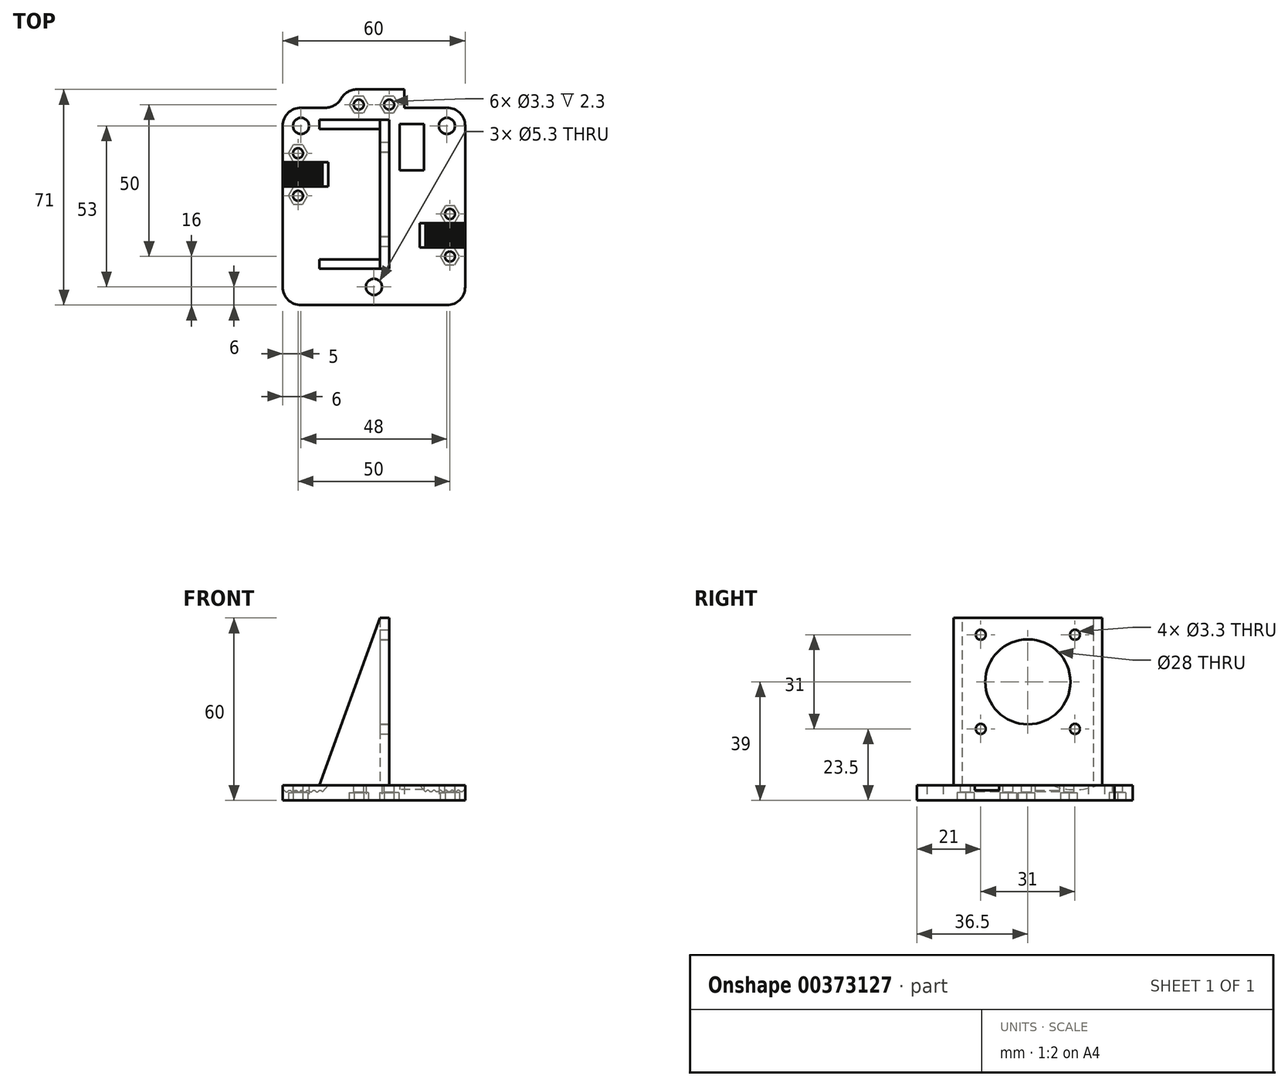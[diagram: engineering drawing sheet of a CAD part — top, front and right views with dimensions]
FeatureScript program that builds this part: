
annotation { "Feature Type Name" : "Feature", "Feature Type Description" : "" }
export const myFeature = defineFeature(function(context is Context, id is Id, definition is map)
    precondition{}
    {
        {
            var Q0;
            Q0=qCreatedBy(makeId("Top.planeOp"),FACE);
            var sketch = newSketch(context, id + "F0", { "sketchPlane" : qUnion([Q0])});
            skLineSegment(sketch, "E0.bottom", {"start": v(0, 0) * mm, "end": v(60, 0) * mm});
            skLineSegment(sketch, "E0.top", {"start": v(0, 65) * mm, "end": v(60, 65) * mm});
            skLineSegment(sketch, "E0.left", {"start": v(0, 0) * mm, "end": v(0, 65) * mm});
            skLineSegment(sketch, "E0.right", {"start": v(60, 0) * mm, "end": v(60, 65) * mm});
            skCircle(sketch, "E1", {"center": v(54, 59) * mm, "radius": 2.65 * mm});
            skCircle(sketch, "E2", {"center": v(6, 59) * mm, "radius": 2.65 * mm});
            skPoint(sketch, "E3.centerSnap0", {"position": v(30, 65) * mm});
            skCircle(sketch, "E4", {"center": v(30, 6) * mm, "radius": 2.65 * mm});
            skPoint(sketch, "E4.centerSnap0", {"position": v(30, 0) * mm});
            skLineSegment(sketch, "E5.bottom", {"start": v(48.77, 52.5) * mm, "end": v(8.77, 52.5) * mm, "construction": true});
            skLineSegment(sketch, "E5.top", {"start": v(48.77, 12.5) * mm, "end": v(8.77, 12.5) * mm, "construction": true});
            skLineSegment(sketch, "E5.left", {"start": v(48.77, 52.5) * mm, "end": v(48.77, 12.5) * mm, "construction": true});
            skLineSegment(sketch, "E5.right", {"start": v(8.77, 52.5) * mm, "end": v(8.77, 12.5) * mm, "construction": true});
            skPoint(sketch, "E5.middle", {"position": v(28.77, 32.5) * mm});
            skPoint(sketch, "E5.middle.positionSnap0", {"position": v(60, 32.5) * mm});
            skPoint(sketch, "E5.centerSnap0", {"position": v(60, 32.5) * mm});
            skSolve(sketch);
        }
        {
            var Q0;
            Q0=qSketchRegion(id+"F0",true);
            extrude(context, id + "F1", {"entities" : qUnion([Q0]), "depth" : 5 * mm});
        }
        {
            var Q0;
            Q0=makeQuery(id+"F1.opExtrude","CAP_FACE",FACE,{"disambiguationData":[OSD([sQuery(id+"F0.wireOp",EDGE,"E0.bottom"),sQuery(id+"F0.wireOp",EDGE,"E0.top"),sQuery(id+"F0.wireOp",EDGE,"E0.left"),sQuery(id+"F0.wireOp",EDGE,"E0.right"),sQuery(id+"F0.wireOp",EDGE,"OE9OXwwY-jkzx-z2IH-hqWW-tGNUMXTa7UCK"),sQuery(id+"F0.wireOp",EDGE,"vX6X2TAe-wOAB-TRkp-mQep-0Cd3F37A3YlU"),sQuery(id+"F0.wireOp",EDGE,"E1"),sQuery(id+"F0.wireOp",EDGE,"E2"),sQuery(id+"F0.wireOp",EDGE,"VI1xqaa2-7410-COSz-W1Es-nAD37MhHaakV.bottom"),sQuery(id+"F0.wireOp",EDGE,"VI1xqaa2-7410-COSz-W1Es-nAD37MhHaakV.top"),sQuery(id+"F0.wireOp",EDGE,"VI1xqaa2-7410-COSz-W1Es-nAD37MhHaakV.left"),sQuery(id+"F0.wireOp",EDGE,"VI1xqaa2-7410-COSz-W1Es-nAD37MhHaakV.right")])],"isStart":false});
            var sketch = newSketch(context, id + "F2", { "sketchPlane" : qUnion([Q0])});
            skLineSegment(sketch, "E6", {"start": v(12, 61) * mm, "end": v(35, 61) * mm});
            skLineSegment(sketch, "E7", {"start": v(35, 61) * mm, "end": v(35, 12) * mm});
            skLineSegment(sketch, "E8", {"start": v(35, 12) * mm, "end": v(12, 12) * mm});
            skLineSegment(sketch, "E9", {"start": v(12, 12) * mm, "end": v(12, 15) * mm});
            skLineSegment(sketch, "E10", {"start": v(12, 15) * mm, "end": v(32, 15) * mm});
            skLineSegment(sketch, "E11", {"start": v(32, 15) * mm, "end": v(32, 58) * mm});
            skLineSegment(sketch, "E12", {"start": v(32, 58) * mm, "end": v(12, 58) * mm});
            skLineSegment(sketch, "E13", {"start": v(12, 58) * mm, "end": v(12, 61) * mm});
            skCircle(sketch, "E14.0", {"center": v(6, 59) * mm, "radius": 2.65 * mm, "construction": true});
            skLineSegment(sketch, "E15.0.0", {"start": v(60, 65) * mm, "end": v(0, 65) * mm, "construction": true});
            skLineSegment(sketch, "E15.0.1", {"start": v(0, 65) * mm, "end": v(0, 0) * mm, "construction": true});
            skLineSegment(sketch, "E15.0.2", {"start": v(0, 0) * mm, "end": v(60, 0) * mm, "construction": true});
            skLineSegment(sketch, "E15.0.3", {"start": v(60, 0) * mm, "end": v(60, 65) * mm, "construction": true});
            skSolve(sketch);
        }
        {
            var Q0;
            Q0=qSketchRegion(id+"F2",true);
            extrude(context, id + "F3", {"entities" : qUnion([Q0]), "operationType" : NewBodyOperationType.ADD, "depth" : 55 * mm});
        }
        {
            var Q0;
            Q0=makeQuery(id+"F3.opExtrude","SWEPT_FACE",FACE,{"disambiguationData":[OSD([sQuery(id+"F2.wireOp",EDGE,"E8")])]});
            var sketch = newSketch(context, id + "F4", { "sketchPlane" : qUnion([Q0])});
            skLineSegment(sketch, "E16.0.1", {"start": v(32, 5) * mm, "end": v(32, 60) * mm, "construction": true});
            skLineSegment(sketch, "E16.0.3", {"start": v(32, 60) * mm, "end": v(32, 5) * mm, "construction": true});
            skLineSegment(sketch, "E17.0.0", {"start": v(32, 5) * mm, "end": v(12, 5) * mm, "construction": true});
            skLineSegment(sketch, "E17.0.2", {"start": v(0, 5) * mm, "end": v(0, 5) * mm});
            skLineSegment(sketch, "E17.0.4", {"start": v(0, 5) * mm, "end": v(60, 5) * mm, "construction": true});
            skLineSegment(sketch, "E17.0.6", {"start": v(60, 5) * mm, "end": v(60, 5) * mm});
            skLineSegment(sketch, "E17.0.8", {"start": v(35, 5) * mm, "end": v(12, 5) * mm, "construction": true});
            skLineSegment(sketch, "E17.0.10", {"start": v(12, 5) * mm, "end": v(32, 5) * mm, "construction": true});
            skLineSegment(sketch, "E18.0.0", {"start": v(12, 5) * mm, "end": v(35, 5) * mm, "construction": true});
            skLineSegment(sketch, "E18.0.1", {"start": v(35, 5) * mm, "end": v(35, 60) * mm, "construction": true});
            skLineSegment(sketch, "E18.0.2", {"start": v(35, 60) * mm, "end": v(12, 60) * mm, "construction": true});
            skLineSegment(sketch, "E18.0.3", {"start": v(12, 60) * mm, "end": v(12, 5) * mm, "construction": true});
            skLineSegment(sketch, "E19", {"start": v(32, 60) * mm, "end": v(12, 5) * mm});
            skLineSegment(sketch, "E20", {"start": v(12, 60) * mm, "end": v(32, 60) * mm});
            skLineSegment(sketch, "E21", {"start": v(12, 60) * mm, "end": v(12, 5) * mm});
            skSolve(sketch);
        }
        {
            var Q0;
            Q0=qSketchRegion(id+"F4",true);
            extrude(context, id + "F5", {"entities" : qUnion([Q0]), "operationType" : NewBodyOperationType.REMOVE, "endBound" : BoundingType.THROUGH_ALL, "oppositeDirection" : true, "depth" : 25 * mm});
        }
        {
            var Q0;
            Q0=makeQuery(id+"F3.opExtrude","SWEPT_FACE",FACE,{"disambiguationData":[OSD([sQuery(id+"F2.wireOp",EDGE,"E7")])]});
            var sketch = newSketch(context, id + "F6", { "sketchPlane" : qUnion([Q0])});
            skCircle(sketch, "E22", {"center": v(36.5, 39) * mm, "radius": 14 * mm});
            skCircle(sketch, "E23", {"center": v(21, 54.5) * mm, "radius": 1.65 * mm});
            skLineSegment(sketch, "E24", {"start": v(44.23, 39) * mm, "end": v(36.5, 39) * mm, "construction": true});
            skLineSegment(sketch, "E25", {"start": v(36.5, 39) * mm, "end": v(36.5, 44.81) * mm, "construction": true});
            skCircle(sketch, "E26.MirrorC", {"center": v(52, 54.5) * mm, "radius": 1.65 * mm});
            skCircle(sketch, "E27.MirrorC", {"center": v(52, 23.5) * mm, "radius": 1.65 * mm});
            skCircle(sketch, "E28.MirrorC", {"center": v(21, 23.5) * mm, "radius": 1.65 * mm});
            skCircle(sketch, "E29", {"center": v(52, 23.5) * mm, "radius": 17 * mm, "construction": true});
            skSolve(sketch);
        }
        {
            var Q0;
            Q0=qSketchRegion(id+"F6",true);
            extrude(context, id + "F7", {"entities" : qUnion([Q0]), "operationType" : NewBodyOperationType.REMOVE, "endBound" : BoundingType.THROUGH_ALL, "oppositeDirection" : true, "depth" : 25 * mm});
        }
        {
            var Q0;
            Q0=makeQuery(id+"F2.imprint","IMPRINT",FACE,{"disambiguationData":[TD([[makeQuery(id+"F2.imprint","IMPRINT",EDGE,{"derivedFrom":sQuery(id+"F2.wireOp",EDGE,"E6")}),1.0]])]});
            var sketch = newSketch(context, id + "F8", { "sketchPlane" : qUnion([Q0])});
            skLineSegment(sketch, "E30.0.0", {"start": v(60, 65) * mm, "end": v(0, 65) * mm, "construction": true});
            skLineSegment(sketch, "E30.0.1", {"start": v(0, 65) * mm, "end": v(0, 0) * mm, "construction": true});
            skLineSegment(sketch, "E30.0.2", {"start": v(0, 0) * mm, "end": v(60, 0) * mm, "construction": true});
            skLineSegment(sketch, "E30.0.3", {"start": v(60, 0) * mm, "end": v(60, 65) * mm, "construction": true});
            skLineSegment(sketch, "E31.bottom", {"start": v(0, 47) * mm, "end": v(15, 47) * mm});
            skLineSegment(sketch, "E31.top", {"start": v(0, 39) * mm, "end": v(15, 39) * mm});
            skLineSegment(sketch, "E31.left", {"start": v(0, 47) * mm, "end": v(0, 39) * mm});
            skLineSegment(sketch, "E31.right", {"start": v(15, 47) * mm, "end": v(15, 39) * mm});
            skLineSegment(sketch, "E32.bottom", {"start": v(60, 27) * mm, "end": v(45, 27) * mm});
            skLineSegment(sketch, "E32.top", {"start": v(60, 19) * mm, "end": v(45, 19) * mm});
            skLineSegment(sketch, "E32.left", {"start": v(60, 27) * mm, "end": v(60, 19) * mm});
            skLineSegment(sketch, "E32.right", {"start": v(45, 27) * mm, "end": v(45, 19) * mm});
            skSolve(sketch);
        }
        {
            var Q0;
            Q0=qSketchRegion(id+"F8",true);
            extrude(context, id + "F9", {"entities" : qUnion([Q0]), "operationType" : NewBodyOperationType.REMOVE, "oppositeDirection" : true, "depth" : 2.25 * mm});
        }
        {
            var Q0;
            Q0=makeQuery(id+"F9.boolean.opBoolean","COPY",FACE,{"derivedFrom":makeQuery(id+"F9.opExtrude","CAP_FACE",FACE,{"disambiguationData":[OSD([sQuery(id+"F8.wireOp",EDGE,"E31.bottom"),sQuery(id+"F8.wireOp",EDGE,"E31.top"),sQuery(id+"F8.wireOp",EDGE,"E31.left"),sQuery(id+"F8.wireOp",EDGE,"E31.right")])],"isStart":false})});
            var sketch = newSketch(context, id + "F10", { "sketchPlane" : qUnion([Q0])});
            skLineSegment(sketch, "E33.bottom", {"start": v(0, 47) * mm, "end": v(1, 47) * mm});
            skLineSegment(sketch, "E33.top", {"start": v(0, 39) * mm, "end": v(1, 39) * mm});
            skLineSegment(sketch, "E33.left", {"start": v(0, 47) * mm, "end": v(0, 39) * mm});
            skLineSegment(sketch, "E33.right", {"start": v(1, 47) * mm, "end": v(1, 39) * mm});
            skLineSegment(sketch, "E34.bottom", {"start": v(1.5, 47) * mm, "end": v(3, 47) * mm});
            skLineSegment(sketch, "E34.top", {"start": v(1.5, 39) * mm, "end": v(3, 39) * mm});
            skLineSegment(sketch, "E34.left", {"start": v(1.5, 47) * mm, "end": v(1.5, 39) * mm});
            skLineSegment(sketch, "E34.right", {"start": v(3, 47) * mm, "end": v(3, 39) * mm});
            skLineSegment(sketch, "E35.bottom", {"start": v(3.5, 47) * mm, "end": v(5, 47) * mm});
            skLineSegment(sketch, "E35.top", {"start": v(3.5, 39) * mm, "end": v(5, 39) * mm});
            skLineSegment(sketch, "E35.left", {"start": v(3.5, 47) * mm, "end": v(3.5, 39) * mm});
            skLineSegment(sketch, "E35.right", {"start": v(5, 47) * mm, "end": v(5, 39) * mm});
            skLineSegment(sketch, "E36.bottom", {"start": v(5.5, 47) * mm, "end": v(7, 47) * mm});
            skLineSegment(sketch, "E36.top", {"start": v(5.5, 39) * mm, "end": v(7, 39) * mm});
            skLineSegment(sketch, "E36.left", {"start": v(5.5, 47) * mm, "end": v(5.5, 39) * mm});
            skLineSegment(sketch, "E36.right", {"start": v(7, 47) * mm, "end": v(7, 39) * mm});
            skLineSegment(sketch, "E37.bottom", {"start": v(7.5, 47) * mm, "end": v(9, 47) * mm});
            skLineSegment(sketch, "E37.top", {"start": v(7.5, 39) * mm, "end": v(9, 39) * mm});
            skLineSegment(sketch, "E37.left", {"start": v(7.5, 47) * mm, "end": v(7.5, 39) * mm});
            skLineSegment(sketch, "E37.right", {"start": v(9, 47) * mm, "end": v(9, 39) * mm});
            skLineSegment(sketch, "E38.bottom", {"start": v(13, 47) * mm, "end": v(11.5, 47) * mm});
            skLineSegment(sketch, "E38.top", {"start": v(13, 39) * mm, "end": v(11.5, 39) * mm});
            skLineSegment(sketch, "E38.left", {"start": v(13, 47) * mm, "end": v(13, 39) * mm});
            skLineSegment(sketch, "E38.right", {"start": v(11.5, 47) * mm, "end": v(11.5, 39) * mm});
            skLineSegment(sketch, "E39.bottom", {"start": v(9.5, 47) * mm, "end": v(11, 47) * mm});
            skLineSegment(sketch, "E39.top", {"start": v(9.5, 39) * mm, "end": v(11, 39) * mm});
            skLineSegment(sketch, "E39.left", {"start": v(9.5, 47) * mm, "end": v(9.5, 39) * mm});
            skLineSegment(sketch, "E39.right", {"start": v(11, 47) * mm, "end": v(11, 39) * mm});
            skSolve(sketch);
        }
        {
            var Q0;
            Q0=qSketchRegion(id+"F10",true);
            extrude(context, id + "F11", {"entities" : qUnion([Q0]), "operationType" : NewBodyOperationType.ADD, "depth" : .5 * mm});
        }
        {
            var Q0;
            Q0=makeQuery(id+"F11.opExtrude","CAP_EDGE",EDGE,{"disambiguationData":[OSD([sQuery(id+"F10.wireOp",EDGE,"E33.right")])],"isStart":false});
            var Q1;
            Q1=makeQuery(id+"F11.opExtrude","CAP_EDGE",EDGE,{"disambiguationData":[OSD([sQuery(id+"F10.wireOp",EDGE,"E34.left")])],"isStart":false});
            var Q2;
            Q2=makeQuery(id+"F11.opExtrude","CAP_EDGE",EDGE,{"disambiguationData":[OSD([sQuery(id+"F10.wireOp",EDGE,"E34.right")])],"isStart":false});
            var Q3;
            Q3=makeQuery(id+"F11.opExtrude","CAP_EDGE",EDGE,{"disambiguationData":[OSD([sQuery(id+"F10.wireOp",EDGE,"E35.left")])],"isStart":false});
            var Q4;
            Q4=makeQuery(id+"F11.opExtrude","CAP_EDGE",EDGE,{"disambiguationData":[OSD([sQuery(id+"F10.wireOp",EDGE,"E35.right")])],"isStart":false});
            var Q5;
            Q5=makeQuery(id+"F11.opExtrude","CAP_EDGE",EDGE,{"disambiguationData":[OSD([sQuery(id+"F10.wireOp",EDGE,"E36.left")])],"isStart":false});
            var Q6;
            Q6=makeQuery(id+"F11.opExtrude","CAP_EDGE",EDGE,{"disambiguationData":[OSD([sQuery(id+"F10.wireOp",EDGE,"E36.right")])],"isStart":false});
            var Q7;
            Q7=makeQuery(id+"F11.opExtrude","CAP_EDGE",EDGE,{"disambiguationData":[OSD([sQuery(id+"F10.wireOp",EDGE,"E37.left")])],"isStart":false});
            var Q8;
            Q8=makeQuery(id+"F11.opExtrude","CAP_EDGE",EDGE,{"disambiguationData":[OSD([sQuery(id+"F10.wireOp",EDGE,"E37.right")])],"isStart":false});
            var Q9;
            Q9=makeQuery(id+"F11.opExtrude","CAP_EDGE",EDGE,{"disambiguationData":[OSD([sQuery(id+"F10.wireOp",EDGE,"E39.right")])],"isStart":false});
            var Q10;
            Q10=makeQuery(id+"F11.opExtrude","CAP_EDGE",EDGE,{"disambiguationData":[OSD([sQuery(id+"F10.wireOp",EDGE,"E39.left")])],"isStart":false});
            var Q11;
            Q11=makeQuery(id+"F11.opExtrude","CAP_EDGE",EDGE,{"disambiguationData":[OSD([sQuery(id+"F10.wireOp",EDGE,"E38.right")])],"isStart":false});
            var Q12;
            Q12=makeQuery(id+"F11.opExtrude","CAP_EDGE",EDGE,{"disambiguationData":[OSD([sQuery(id+"F10.wireOp",EDGE,"E38.left")])],"isStart":false});
            chamfer(context, id + "F12", {"entities" : qUnion([Q0, Q1, Q2, Q3, Q4, Q5, Q6, Q7, Q8, Q9, Q10, Q11, Q12]), "width" : .5 * mm, "tangentPropagation" : true});
        }
        {
            var Q0;
            Q0=makeQuery(id+"F9.boolean.opBoolean","COPY",FACE,{"derivedFrom":makeQuery(id+"F9.opExtrude","SWEPT_FACE",FACE,{"disambiguationData":[OSD([sQuery(id+"F8.wireOp",EDGE,"E31.bottom")])]})});
            var sketch = newSketch(context, id + "F13", { "sketchPlane" : qUnion([Q0])});
            skLineSegment(sketch, "E40", {"start": v(15, 5) * mm, "end": v(15, 2.75) * mm});
            skLineSegment(sketch, "E41", {"start": v(15, 2.75) * mm, "end": v(13, 2.75) * mm});
            skLineSegment(sketch, "E42", {"start": v(13, 2.75) * mm, "end": v(15, 5) * mm});
            skSolve(sketch);
        }
        {
            var Q0;
            Q0=qSketchRegion(id+"F13",true);
            extrude(context, id + "F14", {"entities" : qUnion([Q0]), "operationType" : NewBodyOperationType.ADD, "endBound" : BoundingType.UP_TO_NEXT, "depth" : 25 * mm});
        }
        {
            var Q0;
            Q0=makeQuery(id+"F9.boolean.opBoolean","COPY",FACE,{"derivedFrom":makeQuery(id+"F9.opExtrude","CAP_FACE",FACE,{"disambiguationData":[OSD([sQuery(id+"F8.wireOp",EDGE,"E32.bottom"),sQuery(id+"F8.wireOp",EDGE,"E32.top"),sQuery(id+"F8.wireOp",EDGE,"E32.left"),sQuery(id+"F8.wireOp",EDGE,"E32.right")])],"isStart":false})});
            var sketch = newSketch(context, id + "F15", { "sketchPlane" : qUnion([Q0])});
            skLineSegment(sketch, "E43.bottom", {"start": v(47, 27) * mm, "end": v(48.5, 27) * mm});
            skLineSegment(sketch, "E43.top", {"start": v(47, 19) * mm, "end": v(48.5, 19) * mm});
            skLineSegment(sketch, "E43.left", {"start": v(47, 27) * mm, "end": v(47, 19) * mm});
            skLineSegment(sketch, "E43.right", {"start": v(48.5, 27) * mm, "end": v(48.5, 19) * mm});
            skLineSegment(sketch, "E44.bottom", {"start": v(49, 27) * mm, "end": v(50.5, 27) * mm});
            skLineSegment(sketch, "E44.top", {"start": v(49, 19) * mm, "end": v(50.5, 19) * mm});
            skLineSegment(sketch, "E44.left", {"start": v(49, 27) * mm, "end": v(49, 19) * mm});
            skLineSegment(sketch, "E44.right", {"start": v(50.5, 27) * mm, "end": v(50.5, 19) * mm});
            skLineSegment(sketch, "E45.bottom", {"start": v(51, 27) * mm, "end": v(52.5, 27) * mm});
            skLineSegment(sketch, "E45.top", {"start": v(51, 19) * mm, "end": v(52.5, 19) * mm});
            skLineSegment(sketch, "E45.left", {"start": v(51, 27) * mm, "end": v(51, 19) * mm});
            skLineSegment(sketch, "E45.right", {"start": v(52.5, 27) * mm, "end": v(52.5, 19) * mm});
            skLineSegment(sketch, "E46.bottom", {"start": v(53, 27) * mm, "end": v(54.5, 27) * mm});
            skLineSegment(sketch, "E46.top", {"start": v(53, 19) * mm, "end": v(54.5, 19) * mm});
            skLineSegment(sketch, "E46.left", {"start": v(53, 27) * mm, "end": v(53, 19) * mm});
            skLineSegment(sketch, "E46.right", {"start": v(54.5, 27) * mm, "end": v(54.5, 19) * mm});
            skLineSegment(sketch, "E47.bottom", {"start": v(55, 27) * mm, "end": v(56.5, 27) * mm});
            skLineSegment(sketch, "E47.top", {"start": v(55, 19) * mm, "end": v(56.5, 19) * mm});
            skLineSegment(sketch, "E47.left", {"start": v(55, 27) * mm, "end": v(55, 19) * mm});
            skLineSegment(sketch, "E47.right", {"start": v(56.5, 27) * mm, "end": v(56.5, 19) * mm});
            skLineSegment(sketch, "E48.bottom", {"start": v(57, 27) * mm, "end": v(58.5, 27) * mm});
            skLineSegment(sketch, "E48.top", {"start": v(57, 19) * mm, "end": v(58.5, 19) * mm});
            skLineSegment(sketch, "E48.left", {"start": v(57, 27) * mm, "end": v(57, 19) * mm});
            skLineSegment(sketch, "E48.right", {"start": v(58.5, 27) * mm, "end": v(58.5, 19) * mm});
            skLineSegment(sketch, "E49.bottom", {"start": v(60, 27) * mm, "end": v(59, 27) * mm});
            skLineSegment(sketch, "E49.top", {"start": v(60, 19) * mm, "end": v(59, 19) * mm});
            skLineSegment(sketch, "E49.left", {"start": v(60, 27) * mm, "end": v(60, 19) * mm});
            skLineSegment(sketch, "E49.right", {"start": v(59, 27) * mm, "end": v(59, 19) * mm});
            skSolve(sketch);
        }
        {
            var Q0;
            Q0=qSketchRegion(id+"F15",true);
            extrude(context, id + "F16", {"entities" : qUnion([Q0]), "operationType" : NewBodyOperationType.ADD, "depth" : .5 * mm});
        }
        {
            var Q0;
            Q0=makeQuery(id+"F16.opExtrude","CAP_EDGE",EDGE,{"disambiguationData":[OSD([sQuery(id+"F15.wireOp",EDGE,"E49.right")])],"isStart":false});
            var Q1;
            Q1=makeQuery(id+"F16.opExtrude","CAP_EDGE",EDGE,{"disambiguationData":[OSD([sQuery(id+"F15.wireOp",EDGE,"E48.right")])],"isStart":false});
            var Q2;
            Q2=makeQuery(id+"F16.opExtrude","CAP_EDGE",EDGE,{"disambiguationData":[OSD([sQuery(id+"F15.wireOp",EDGE,"E48.left")])],"isStart":false});
            var Q3;
            Q3=makeQuery(id+"F16.opExtrude","CAP_EDGE",EDGE,{"disambiguationData":[OSD([sQuery(id+"F15.wireOp",EDGE,"E47.right")])],"isStart":false});
            var Q4;
            Q4=makeQuery(id+"F16.opExtrude","CAP_EDGE",EDGE,{"disambiguationData":[OSD([sQuery(id+"F15.wireOp",EDGE,"E47.left")])],"isStart":false});
            var Q5;
            Q5=makeQuery(id+"F16.opExtrude","CAP_EDGE",EDGE,{"disambiguationData":[OSD([sQuery(id+"F15.wireOp",EDGE,"E46.right")])],"isStart":false});
            var Q6;
            Q6=makeQuery(id+"F16.opExtrude","CAP_EDGE",EDGE,{"disambiguationData":[OSD([sQuery(id+"F15.wireOp",EDGE,"E46.left")])],"isStart":false});
            var Q7;
            Q7=makeQuery(id+"F16.opExtrude","CAP_EDGE",EDGE,{"disambiguationData":[OSD([sQuery(id+"F15.wireOp",EDGE,"E45.right")])],"isStart":false});
            var Q8;
            Q8=makeQuery(id+"F16.opExtrude","CAP_EDGE",EDGE,{"disambiguationData":[OSD([sQuery(id+"F15.wireOp",EDGE,"E45.left")])],"isStart":false});
            var Q9;
            Q9=makeQuery(id+"F16.opExtrude","CAP_EDGE",EDGE,{"disambiguationData":[OSD([sQuery(id+"F15.wireOp",EDGE,"E44.right")])],"isStart":false});
            var Q10;
            Q10=makeQuery(id+"F16.opExtrude","CAP_EDGE",EDGE,{"disambiguationData":[OSD([sQuery(id+"F15.wireOp",EDGE,"E44.left")])],"isStart":false});
            var Q11;
            Q11=makeQuery(id+"F16.opExtrude","CAP_EDGE",EDGE,{"disambiguationData":[OSD([sQuery(id+"F15.wireOp",EDGE,"E43.right")])],"isStart":false});
            var Q12;
            Q12=makeQuery(id+"F16.opExtrude","CAP_EDGE",EDGE,{"disambiguationData":[OSD([sQuery(id+"F15.wireOp",EDGE,"E43.left")])],"isStart":false});
            chamfer(context, id + "F17", {"entities" : qUnion([Q0, Q1, Q2, Q3, Q4, Q5, Q6, Q7, Q8, Q9, Q10, Q11, Q12]), "width" : .5 * mm, "tangentPropagation" : true});
        }
        {
            var Q0;
            Q0=makeQuery(id+"F9.boolean.opBoolean","COPY",FACE,{"derivedFrom":makeQuery(id+"F9.opExtrude","SWEPT_FACE",FACE,{"disambiguationData":[OSD([sQuery(id+"F8.wireOp",EDGE,"E32.bottom")])]})});
            var sketch = newSketch(context, id + "F18", { "sketchPlane" : qUnion([Q0])});
            skLineSegment(sketch, "E50", {"start": v(45, 2.75) * mm, "end": v(45, 5) * mm});
            skLineSegment(sketch, "E51", {"start": v(45, 5) * mm, "end": v(47, 2.75) * mm});
            skLineSegment(sketch, "E52", {"start": v(45, 2.75) * mm, "end": v(47, 2.75) * mm});
            skSolve(sketch);
        }
        {
            var Q0;
            Q0=qSketchRegion(id+"F18",true);
            extrude(context, id + "F19", {"entities" : qUnion([Q0]), "operationType" : NewBodyOperationType.ADD, "endBound" : BoundingType.UP_TO_NEXT, "depth" : 25 * mm});
        }
        {
            var Q0;
            Q0=makeQuery(id+"F1.opExtrude","SWEPT_EDGE",EDGE,{"disambiguationData":[OSD([sQuery(id+"F0.wireOp",EDGE,"E0.top"),sQuery(id+"F0.wireOp",EDGE,"E0.right")])]});
            var Q1;
            Q1=makeQuery(id+"F1.opExtrude","SWEPT_EDGE",EDGE,{"disambiguationData":[OSD([sQuery(id+"F0.wireOp",EDGE,"E0.bottom"),sQuery(id+"F0.wireOp",EDGE,"E0.right")])]});
            var Q2;
            Q2=makeQuery(id+"F1.opExtrude","SWEPT_EDGE",EDGE,{"disambiguationData":[OSD([sQuery(id+"F0.wireOp",EDGE,"E0.bottom"),sQuery(id+"F0.wireOp",EDGE,"E0.left")])]});
            var Q3;
            Q3=makeQuery(id+"F1.opExtrude","SWEPT_EDGE",EDGE,{"disambiguationData":[OSD([sQuery(id+"F0.wireOp",EDGE,"E0.top"),sQuery(id+"F0.wireOp",EDGE,"E0.left")])]});
            fillet(context, id + "F20", {"entities" : qUnion([Q0, Q1, Q2, Q3]), "radius" : 6 * mm, "tangentPropagation" : true, "allowEdgeOverflow" : false});
        }
        {
            var Q0;
            Q0=makeQuery(id+"F6.imprint","IMPRINT",FACE,{"disambiguationData":[TD([[makeQuery(id+"F6.imprint","IMPRINT",EDGE,{"derivedFrom":sQuery(id+"F6.wireOp",EDGE,"E22")}),-1.0]])]});
            cPlane(context, id + "F21", {"entities" : qUnion([Q0]), "cplaneType" : CPlaneType.OFFSET, "offset" : 3.5 * mm, "width" : 150 * mm, "height" : 150 * mm});
        }
        {
            var Q0;
            Q0=qCreatedBy(id+"F21.planeOp",FACE);
            var sketch = newSketch(context, id + "F22", { "sketchPlane" : qUnion([Q0])});
            skCircle(sketch, "E53.0", {"center": v(52, 23.5) * mm, "radius": 17 * mm, "construction": true});
            skCircle(sketch, "E54", {"center": v(52, 23.5) * mm, "radius": 20 * mm});
            skSolve(sketch);
        }
        {
            var Q0;
            Q0=qSketchRegion(id+"F22",true);
            extrude(context, id + "F23", {"entities" : qUnion([Q0]), "operationType" : NewBodyOperationType.REMOVE, "depth" : 8 * mm});
        }
        {
            var Q0;
            Q0=makeQuery(id+"F2.imprint","IMPRINT",FACE,{"disambiguationData":[TD([[makeQuery(id+"F2.imprint","IMPRINT",EDGE,{"derivedFrom":sQuery(id+"F2.wireOp",EDGE,"E6")}),1.0]])]});
            var sketch = newSketch(context, id + "F24", { "sketchPlane" : qUnion([Q0])});
            skLineSegment(sketch, "E55.0.0", {"start": v(60, 65) * mm, "end": v(0, 65) * mm, "construction": true});
            skLineSegment(sketch, "E55.0.1", {"start": v(0, 65) * mm, "end": v(0, 0) * mm, "construction": true});
            skLineSegment(sketch, "E55.0.2", {"start": v(0, 0) * mm, "end": v(60, 0) * mm, "construction": true});
            skLineSegment(sketch, "E55.0.3", {"start": v(60, 0) * mm, "end": v(60, 65) * mm, "construction": true});
            skCircle(sketch, "E56", {"center": v(5, 50) * mm, "radius": 1.65 * mm});
            skCircle(sketch, "E57", {"center": v(5, 36) * mm, "radius": 1.65 * mm});
            skCircle(sketch, "E58", {"center": v(55, 30) * mm, "radius": 1.65 * mm});
            skCircle(sketch, "E59", {"center": v(55, 16) * mm, "radius": 1.65 * mm});
            skLineSegment(sketch, "E60.bottom", {"start": v(30, 16) * mm, "end": v(55, 16) * mm, "construction": true});
            skLineSegment(sketch, "E60.top", {"start": v(30, -44) * mm, "end": v(55, -44) * mm, "construction": true});
            skLineSegment(sketch, "E60.left", {"start": v(30, 16) * mm, "end": v(30, -44) * mm, "construction": true});
            skLineSegment(sketch, "E60.right", {"start": v(55, 16) * mm, "end": v(55, -44) * mm, "construction": true});
            skLineSegment(sketch, "E61.bottom", {"start": v(45, -44) * mm, "end": v(50, -44) * mm, "construction": true});
            skLineSegment(sketch, "E61.top", {"start": v(45, -49) * mm, "end": v(50, -49) * mm, "construction": true});
            skLineSegment(sketch, "E61.left", {"start": v(45, -44) * mm, "end": v(45, -49) * mm, "construction": true});
            skLineSegment(sketch, "E61.right", {"start": v(50, -44) * mm, "end": v(50, -49) * mm, "construction": true});
            skLineSegment(sketch, "E62", {"start": v(61.03, -19.82) * mm, "end": v(99.67, -30.17) * mm});
            skLineSegment(sketch, "E63", {"start": v(99.67, -30.17) * mm, "end": v(104.84, -10.85) * mm});
            skLineSegment(sketch, "E64", {"start": v(104.84, -10.85) * mm, "end": v(66.2, -0.5) * mm});
            skLineSegment(sketch, "E65", {"start": v(66.2, -0.5) * mm, "end": v(61.03, -19.82) * mm});
            skLineSegment(sketch, "E66", {"start": v(61.03, -19.82) * mm, "end": v(67, -42.12) * mm});
            skLineSegment(sketch, "E67", {"start": v(67, -42.12) * mm, "end": v(83.34, -46.5) * mm});
            skLineSegment(sketch, "E68", {"start": v(83.34, -46.5) * mm, "end": v(99.67, -30.17) * mm});
            skLineSegment(sketch, "E69", {"start": v(104.84, -10.85) * mm, "end": v(106.14, -6.02) * mm});
            skLineSegment(sketch, "E70", {"start": v(106.14, -6.02) * mm, "end": v(67.5, 4.33) * mm});
            skLineSegment(sketch, "E71", {"start": v(67.5, 4.33) * mm, "end": v(66.2, -0.5) * mm});
            skCircle(sketch, "E72", {"center": v(67.5, 10.23) * mm, "radius": 4 * mm});
            skLineSegment(sketch, "E73", {"start": v(67.5, 4.33) * mm, "end": v(67.5, 10.23) * mm});
            skLineSegment(sketch, "E74.MirrorCS", {"start": v(23.48, -29) * mm, "end": v(-16.52, -29) * mm});
            skLineSegment(sketch, "E75.MirrorCS", {"start": v(23.48, -9) * mm, "end": v(23.48, -29) * mm});
            skLineSegment(sketch, "E76.MirrorCS", {"start": v(23.48, -4) * mm, "end": v(23.48, -9) * mm});
            skLineSegment(sketch, "E77.MirrorCS", {"start": v(-16.52, -9) * mm, "end": v(-16.52, -4) * mm});
            skLineSegment(sketch, "E78.MirrorCS", {"start": v(-16.52, -4) * mm, "end": v(23.48, -4) * mm});
            skLineSegment(sketch, "E79.MirrorCS", {"start": v(-16.52, -29) * mm, "end": v(-16.52, -9) * mm});
            skLineSegment(sketch, "E80.MirrorCS", {"start": v(-16.52, -9) * mm, "end": v(23.48, -9) * mm});
            skLineSegment(sketch, "E81", {"start": v(3.48, -4) * mm, "end": v(3.48, -29) * mm, "construction": true});
            skCircle(sketch, "E82.MirrorC", {"center": v(-16.52, 2.1) * mm, "radius": 4 * mm});
            skLineSegment(sketch, "E83.MirrorCS", {"start": v(-16.52, -4) * mm, "end": v(-16.52, 2.1) * mm});
            skLineSegment(sketch, "E84", {"start": v(-16.52, -29) * mm, "end": v(7.07, -46.5) * mm});
            skLineSegment(sketch, "E85", {"start": v(7.07, -46.5) * mm, "end": v(23.5, -42.12) * mm});
            skLineSegment(sketch, "E86", {"start": v(23.5, -42.12) * mm, "end": v(23.48, -29) * mm});
            skSolve(sketch);
        }
        {
            var Q0;
            Q0=qSketchRegion(id+"F24",true);
            extrude(context, id + "F25", {"entities" : qUnion([Q0]), "operationType" : NewBodyOperationType.REMOVE, "oppositeDirection" : true, "depth" : 2.3 * mm});
        }
        {
            var Q0;
            Q0=makeQuery(id+"F1.opExtrude","CAP_FACE",FACE,{"disambiguationData":[OSD([sQuery(id+"F0.wireOp",EDGE,"E0.bottom"),sQuery(id+"F0.wireOp",EDGE,"E0.top"),sQuery(id+"F0.wireOp",EDGE,"E0.left"),sQuery(id+"F0.wireOp",EDGE,"E0.right"),sQuery(id+"F0.wireOp",EDGE,"E1"),sQuery(id+"F0.wireOp",EDGE,"E2"),sQuery(id+"F0.wireOp",EDGE,"E4")])],"isStart":true});
            var sketch = newSketch(context, id + "F26", { "sketchPlane" : qUnion([Q0])});
            skLineSegment(sketch, "E87.0.0", {"start": v(54, -65) * mm, "end": v(6, -65) * mm, "construction": true});
            skArc(sketch, "E87.0.1", {"start": v(6, -65) * mm, "mid": v(1.76, -63.24) * mm, "end": v(0, -59) * mm, "construction": true});
            skLineSegment(sketch, "E87.0.2", {"start": v(0, -59) * mm, "end": v(0, -47) * mm, "construction": true});
            skLineSegment(sketch, "E87.0.3", {"start": v(0, -47) * mm, "end": v(15, -47) * mm, "construction": true});
            skLineSegment(sketch, "E87.0.4", {"start": v(15, -47) * mm, "end": v(15, -39) * mm, "construction": true});
            skLineSegment(sketch, "E87.0.5", {"start": v(15, -39) * mm, "end": v(0, -39) * mm, "construction": true});
            skLineSegment(sketch, "E87.0.6", {"start": v(0, -39) * mm, "end": v(0, -6) * mm, "construction": true});
            skArc(sketch, "E87.0.7", {"start": v(0, -6) * mm, "mid": v(1.76, -1.76) * mm, "end": v(6, 0) * mm, "construction": true});
            skLineSegment(sketch, "E87.0.8", {"start": v(6, 0) * mm, "end": v(54, 0) * mm, "construction": true});
            skArc(sketch, "E87.0.9", {"start": v(54, 0) * mm, "mid": v(58.24, -1.76) * mm, "end": v(60, -6) * mm, "construction": true});
            skLineSegment(sketch, "E87.0.10", {"start": v(60, -6) * mm, "end": v(60, -19) * mm, "construction": true});
            skLineSegment(sketch, "E87.0.11", {"start": v(60, -19) * mm, "end": v(45, -19) * mm, "construction": true});
            skLineSegment(sketch, "E87.0.12", {"start": v(45, -19) * mm, "end": v(45, -27) * mm, "construction": true});
            skLineSegment(sketch, "E87.0.13", {"start": v(45, -27) * mm, "end": v(60, -27) * mm, "construction": true});
            skLineSegment(sketch, "E87.0.14", {"start": v(60, -27) * mm, "end": v(60, -59) * mm, "construction": true});
            skArc(sketch, "E87.0.15", {"start": v(60, -59) * mm, "mid": v(58.24, -63.24) * mm, "end": v(54, -65) * mm, "construction": true});
            skCircle(sketch, "E88.0", {"center": v(55, -30) * mm, "radius": 1.65 * mm, "construction": true});
            skCircle(sketch, "E89.0", {"center": v(55, -16) * mm, "radius": 1.65 * mm, "construction": true});
            skPoint(sketch, "E90.0", {"position": v(48.5, -19) * mm});
            skPoint(sketch, "E91.0", {"position": v(47, -19) * mm});
            skCircle(sketch, "E92.0", {"center": v(5, -50) * mm, "radius": 1.65 * mm, "construction": true});
            skCircle(sketch, "E93.0", {"center": v(5, -36) * mm, "radius": 1.65 * mm, "construction": true});
            skCircle(sketch, "E94.cCircle", {"center": v(55, -16) * mm, "radius": 2.75 * mm, "construction": true});
            skLineSegment(sketch, "E94.0", {"start": v(53.41, -13.25) * mm, "end": v(56.59, -13.25) * mm});
            skLineSegment(sketch, "E94.1", {"start": v(56.59, -13.25) * mm, "end": v(58.18, -16) * mm});
            skLineSegment(sketch, "E94.2", {"start": v(58.18, -16) * mm, "end": v(56.59, -18.75) * mm});
            skLineSegment(sketch, "E94.3", {"start": v(56.59, -18.75) * mm, "end": v(53.41, -18.75) * mm});
            skLineSegment(sketch, "E94.4", {"start": v(53.41, -18.75) * mm, "end": v(51.82, -16) * mm});
            skLineSegment(sketch, "E94.5", {"start": v(51.82, -16) * mm, "end": v(53.41, -13.25) * mm});
            skPoint(sketch, "E94.0.midPoint", {"position": v(55, -13.25) * mm});
            skCircle(sketch, "E95.cCircle", {"center": v(55, -30) * mm, "radius": 2.75 * mm, "construction": true});
            skLineSegment(sketch, "E95.0", {"start": v(56.59, -32.75) * mm, "end": v(53.41, -32.75) * mm});
            skLineSegment(sketch, "E95.1", {"start": v(53.41, -32.75) * mm, "end": v(51.82, -30) * mm});
            skLineSegment(sketch, "E95.2", {"start": v(51.82, -30) * mm, "end": v(53.41, -27.25) * mm});
            skLineSegment(sketch, "E95.3", {"start": v(53.41, -27.25) * mm, "end": v(56.59, -27.25) * mm});
            skLineSegment(sketch, "E95.4", {"start": v(56.59, -27.25) * mm, "end": v(58.18, -30) * mm});
            skLineSegment(sketch, "E95.5", {"start": v(58.18, -30) * mm, "end": v(56.59, -32.75) * mm});
            skPoint(sketch, "E95.0.midPoint", {"position": v(55, -32.75) * mm});
            skCircle(sketch, "E96.cCircle", {"center": v(5, -50) * mm, "radius": 2.75 * mm, "construction": true});
            skLineSegment(sketch, "E96.0", {"start": v(6.59, -52.75) * mm, "end": v(3.41, -52.75) * mm});
            skLineSegment(sketch, "E96.1", {"start": v(3.41, -52.75) * mm, "end": v(1.82, -50) * mm});
            skLineSegment(sketch, "E96.2", {"start": v(1.82, -50) * mm, "end": v(3.41, -47.25) * mm});
            skLineSegment(sketch, "E96.3", {"start": v(3.41, -47.25) * mm, "end": v(6.59, -47.25) * mm});
            skLineSegment(sketch, "E96.4", {"start": v(6.59, -47.25) * mm, "end": v(8.18, -50) * mm});
            skLineSegment(sketch, "E96.5", {"start": v(8.18, -50) * mm, "end": v(6.59, -52.75) * mm});
            skPoint(sketch, "E96.0.midPoint", {"position": v(5, -52.75) * mm});
            skCircle(sketch, "E97.cCircle", {"center": v(5, -36) * mm, "radius": 2.75 * mm, "construction": true});
            skLineSegment(sketch, "E97.0", {"start": v(6.59, -38.75) * mm, "end": v(3.41, -38.75) * mm});
            skLineSegment(sketch, "E97.1", {"start": v(3.41, -38.75) * mm, "end": v(1.82, -36) * mm});
            skLineSegment(sketch, "E97.2", {"start": v(1.82, -36) * mm, "end": v(3.41, -33.25) * mm});
            skLineSegment(sketch, "E97.3", {"start": v(3.41, -33.25) * mm, "end": v(6.59, -33.25) * mm});
            skLineSegment(sketch, "E97.4", {"start": v(6.59, -33.25) * mm, "end": v(8.18, -36) * mm});
            skLineSegment(sketch, "E97.5", {"start": v(8.18, -36) * mm, "end": v(6.59, -38.75) * mm});
            skPoint(sketch, "E97.0.midPoint", {"position": v(5, -38.75) * mm});
            skSolve(sketch);
        }
        {
            var Q0;
            Q0=qSketchRegion(id+"F26",true);
            extrude(context, id + "F27", {"entities" : qUnion([Q0]), "operationType" : NewBodyOperationType.REMOVE, "oppositeDirection" : true, "depth" : 2.5 * mm});
        }
        {
            var Q0;
            Q0=makeQuery(id+"F1.opExtrude","CAP_FACE",FACE,{"disambiguationData":[OSD([sQuery(id+"F0.wireOp",EDGE,"E0.bottom"),sQuery(id+"F0.wireOp",EDGE,"E0.top"),sQuery(id+"F0.wireOp",EDGE,"E0.left"),sQuery(id+"F0.wireOp",EDGE,"E0.right"),sQuery(id+"F0.wireOp",EDGE,"E1"),sQuery(id+"F0.wireOp",EDGE,"E2"),sQuery(id+"F0.wireOp",EDGE,"E4")])],"isStart":false});
            var sketch = newSketch(context, id + "F28", { "sketchPlane" : qUnion([Q0])});
            skLineSegment(sketch, "E98.0.0", {"start": v(54, 65) * mm, "end": v(6, 65) * mm, "construction": true});
            skArc(sketch, "E98.0.1", {"start": v(6, 65) * mm, "mid": v(1.76, 63.24) * mm, "end": v(0, 59) * mm, "construction": true});
            skLineSegment(sketch, "E98.0.2", {"start": v(0, 59) * mm, "end": v(0, 47) * mm, "construction": true});
            skLineSegment(sketch, "E98.0.3", {"start": v(0, 47) * mm, "end": v(15, 47) * mm, "construction": true});
            skLineSegment(sketch, "E98.0.4", {"start": v(15, 47) * mm, "end": v(15, 39) * mm, "construction": true});
            skLineSegment(sketch, "E98.0.5", {"start": v(15, 39) * mm, "end": v(0, 39) * mm, "construction": true});
            skLineSegment(sketch, "E98.0.6", {"start": v(0, 39) * mm, "end": v(0, 6) * mm, "construction": true});
            skArc(sketch, "E98.0.7", {"start": v(0, 6) * mm, "mid": v(1.76, 1.76) * mm, "end": v(6, 0) * mm, "construction": true});
            skLineSegment(sketch, "E98.0.8", {"start": v(6, 0) * mm, "end": v(54, 0) * mm, "construction": true});
            skArc(sketch, "E98.0.9", {"start": v(54, 0) * mm, "mid": v(58.24, 1.76) * mm, "end": v(60, 6) * mm, "construction": true});
            skLineSegment(sketch, "E98.0.10", {"start": v(60, 6) * mm, "end": v(60, 19) * mm, "construction": true});
            skLineSegment(sketch, "E98.0.11", {"start": v(60, 19) * mm, "end": v(45, 19) * mm, "construction": true});
            skLineSegment(sketch, "E98.0.12", {"start": v(45, 19) * mm, "end": v(45, 27) * mm, "construction": true});
            skLineSegment(sketch, "E98.0.13", {"start": v(45, 27) * mm, "end": v(60, 27) * mm, "construction": true});
            skLineSegment(sketch, "E98.0.14", {"start": v(60, 27) * mm, "end": v(60, 59) * mm, "construction": true});
            skArc(sketch, "E98.0.15", {"start": v(60, 59) * mm, "mid": v(58.24, 63.24) * mm, "end": v(54, 65) * mm, "construction": true});
            skLineSegment(sketch, "E99.0", {"start": v(12, 61) * mm, "end": v(32, 61) * mm, "construction": true});
            skSolve(sketch);
        }
        {
            var Q0;
            Q0=makeQuery(id+"F1.opExtrude","CAP_FACE",FACE,{"disambiguationData":[OSD([sQuery(id+"F0.wireOp",EDGE,"E0.bottom"),sQuery(id+"F0.wireOp",EDGE,"E0.top"),sQuery(id+"F0.wireOp",EDGE,"E0.left"),sQuery(id+"F0.wireOp",EDGE,"E0.right"),sQuery(id+"F0.wireOp",EDGE,"E1"),sQuery(id+"F0.wireOp",EDGE,"E2"),sQuery(id+"F0.wireOp",EDGE,"E4")])],"isStart":true});
            var sketch = newSketch(context, id + "F29", { "sketchPlane" : qUnion([Q0])});
            skLineSegment(sketch, "E100.bottom", {"start": v(40, -65) * mm, "end": v(20, -65) * mm});
            skLineSegment(sketch, "E100.top", {"start": v(40, -71) * mm, "end": v(20, -71) * mm});
            skLineSegment(sketch, "E100.left", {"start": v(40, -65) * mm, "end": v(40, -71) * mm});
            skLineSegment(sketch, "E100.right", {"start": v(20, -65) * mm, "end": v(20, -71) * mm});
            skSolve(sketch);
        }
        {
            var Q0;
            Q0=qSketchRegion(id+"F29",true);
            var Q1;
            Q1=makeQuery(id+"F1.opExtrude","CAP_FACE",FACE,{"disambiguationData":[OSD([sQuery(id+"F0.wireOp",EDGE,"E0.bottom"),sQuery(id+"F0.wireOp",EDGE,"E0.top"),sQuery(id+"F0.wireOp",EDGE,"E0.left"),sQuery(id+"F0.wireOp",EDGE,"E0.right"),sQuery(id+"F0.wireOp",EDGE,"E1"),sQuery(id+"F0.wireOp",EDGE,"E2"),sQuery(id+"F0.wireOp",EDGE,"E4")])],"isStart":false});
            extrude(context, id + "F30", {"entities" : qUnion([Q0]), "operationType" : NewBodyOperationType.ADD, "endBound" : BoundingType.UP_TO_SURFACE, "oppositeDirection" : true, "endBoundEntityFace" : qUnion([Q1]), "depth" : 25 * mm});
        }
        {
            var Q0;
            {var subQ0=sQuery(id+"F0.wireOp",EDGE,"E4");var subQ1=sQuery(id+"F0.wireOp",EDGE,"E2");var subQ2=sQuery(id+"F0.wireOp",EDGE,"E1");var subQ3=sQuery(id+"F0.wireOp",EDGE,"E0.right");var subQ4=sQuery(id+"F0.wireOp",EDGE,"E0.left");var subQ5=sQuery(id+"F0.wireOp",EDGE,"E0.top");var subQ6=sQuery(id+"F0.wireOp",EDGE,"E0.bottom");Q0=makeQuery(id+"F30.boolean.opBoolean","MERGE",FACE,{"derivedFrom":[makeQuery(id+"F1.opExtrude","CAP_FACE",FACE,{"disambiguationData":[OSD([subQ6,subQ5,subQ4,subQ3,subQ2,subQ1,subQ0])],"isStart":false}),makeQuery(id+"F30.opExtrude","CAP_FACE",FACE,{"disambiguationData":[OSD([subQ6,subQ5,subQ4,subQ3,subQ2,subQ1,subQ0])],"isStart":false})]});}
            var sketch = newSketch(context, id + "F31", { "sketchPlane" : qUnion([Q0])});
            skCircle(sketch, "E101", {"center": v(25, 66) * mm, "radius": 1.65 * mm});
            skCircle(sketch, "E102", {"center": v(35, 66) * mm, "radius": 1.65 * mm});
            skSolve(sketch);
        }
        {
            var Q0;
            Q0=makeQuery(id+"F30.boolean.opBoolean","MERGE",FACE,{"derivedFrom":[makeQuery(id+"F1.opExtrude","CAP_FACE",FACE,{"disambiguationData":[OSD([sQuery(id+"F0.wireOp",EDGE,"E0.bottom"),sQuery(id+"F0.wireOp",EDGE,"E0.top"),sQuery(id+"F0.wireOp",EDGE,"E0.left"),sQuery(id+"F0.wireOp",EDGE,"E0.right"),sQuery(id+"F0.wireOp",EDGE,"E1"),sQuery(id+"F0.wireOp",EDGE,"E2"),sQuery(id+"F0.wireOp",EDGE,"E4")])],"isStart":true}),makeQuery(id+"F30.opExtrude","CAP_FACE",FACE,{"disambiguationData":[OSD([sQuery(id+"F29.wireOp",EDGE,"E100.bottom"),sQuery(id+"F29.wireOp",EDGE,"E100.top"),sQuery(id+"F29.wireOp",EDGE,"E100.left"),sQuery(id+"F29.wireOp",EDGE,"E100.right")])],"isStart":true})]});
            var sketch = newSketch(context, id + "F32", { "sketchPlane" : qUnion([Q0])});
            skCircle(sketch, "E103.0", {"center": v(25, -66) * mm, "radius": 1.65 * mm, "construction": true});
            skCircle(sketch, "E104.0", {"center": v(35, -66) * mm, "radius": 1.65 * mm, "construction": true});
            skCircle(sketch, "E105.cCircle", {"center": v(25, -66) * mm, "radius": 2.75 * mm, "construction": true});
            skLineSegment(sketch, "E105.0", {"start": v(23.41, -63.25) * mm, "end": v(26.59, -63.25) * mm});
            skLineSegment(sketch, "E105.1", {"start": v(26.59, -63.25) * mm, "end": v(28.18, -66) * mm});
            skLineSegment(sketch, "E105.2", {"start": v(28.18, -66) * mm, "end": v(26.59, -68.75) * mm});
            skLineSegment(sketch, "E105.3", {"start": v(26.59, -68.75) * mm, "end": v(23.41, -68.75) * mm});
            skLineSegment(sketch, "E105.4", {"start": v(23.41, -68.75) * mm, "end": v(21.82, -66) * mm});
            skLineSegment(sketch, "E105.5", {"start": v(21.82, -66) * mm, "end": v(23.41, -63.25) * mm});
            skPoint(sketch, "E105.0.midPoint", {"position": v(25, -63.25) * mm});
            skCircle(sketch, "E106.cCircle", {"center": v(35, -66) * mm, "radius": 2.75 * mm, "construction": true});
            skLineSegment(sketch, "E106.0", {"start": v(33.41, -63.25) * mm, "end": v(36.59, -63.25) * mm});
            skLineSegment(sketch, "E106.1", {"start": v(36.59, -63.25) * mm, "end": v(38.18, -66) * mm});
            skLineSegment(sketch, "E106.2", {"start": v(38.18, -66) * mm, "end": v(36.59, -68.75) * mm});
            skLineSegment(sketch, "E106.3", {"start": v(36.59, -68.75) * mm, "end": v(33.41, -68.75) * mm});
            skLineSegment(sketch, "E106.4", {"start": v(33.41, -68.75) * mm, "end": v(31.82, -66) * mm});
            skLineSegment(sketch, "E106.5", {"start": v(31.82, -66) * mm, "end": v(33.41, -63.25) * mm});
            skPoint(sketch, "E106.0.midPoint", {"position": v(35, -63.25) * mm});
            skSolve(sketch);
        }
        {
            var Q0;
            Q0=qSketchRegion(id+"F31",true);
            extrude(context, id + "F33", {"entities" : qUnion([Q0]), "operationType" : NewBodyOperationType.REMOVE, "oppositeDirection" : true, "depth" : 2.3 * mm});
        }
        {
            var Q0;
            Q0=qSketchRegion(id+"F32",true);
            extrude(context, id + "F34", {"entities" : qUnion([Q0]), "operationType" : NewBodyOperationType.REMOVE, "oppositeDirection" : true, "depth" : 2.5 * mm});
        }
        {
            var Q0;
            Q0=makeQuery(id+"F30.opExtrude","SWEPT_EDGE",EDGE,{"disambiguationData":[OSD([sQuery(id+"F0.wireOp",EDGE,"E0.top"),sQuery(id+"F29.wireOp",EDGE,"E100.bottom"),sQuery(id+"F29.wireOp",EDGE,"E100.right")])]});
            var Q1;
            Q1=makeQuery(id+"F30.opExtrude","SWEPT_EDGE",EDGE,{"disambiguationData":[OSD([sQuery(id+"F0.wireOp",EDGE,"E0.top"),sQuery(id+"F29.wireOp",EDGE,"E100.bottom"),sQuery(id+"F29.wireOp",EDGE,"E100.left")])]});
            fillet(context, id + "F35", {"entities" : qUnion([Q0, Q1]), "radius" : 6 * mm, "tangentPropagation" : true, "allowEdgeOverflow" : false});
        }
        {
            var Q0;
            Q0=makeQuery(id+"F35.opFillet","BLEND_EDGE",EDGE,{"blendedFrom":[makeQuery(id+"F30.opExtrude","SWEPT_EDGE",EDGE,{"disambiguationData":[OSD([sQuery(id+"F0.wireOp",EDGE,"E0.top"),sQuery(id+"F29.wireOp",EDGE,"E100.bottom"),sQuery(id+"F29.wireOp",EDGE,"E100.left")])]}),makeQuery(id+"F30.opExtrude","SWEPT_FACE",FACE,{"disambiguationData":[OSD([sQuery(id+"F29.wireOp",EDGE,"E100.top")])]})],"blendedInto":[makeQuery(id+"F30.opExtrude","SWEPT_FACE",FACE,{"disambiguationData":[OSD([sQuery(id+"F29.wireOp",EDGE,"E100.top")])]})]});
            var Q1;
            Q1=makeQuery(id+"F35.opFillet","BLEND_EDGE",EDGE,{"blendedFrom":[makeQuery(id+"F30.opExtrude","SWEPT_EDGE",EDGE,{"disambiguationData":[OSD([sQuery(id+"F0.wireOp",EDGE,"E0.top"),sQuery(id+"F29.wireOp",EDGE,"E100.bottom"),sQuery(id+"F29.wireOp",EDGE,"E100.right")])]}),makeQuery(id+"F30.opExtrude","SWEPT_FACE",FACE,{"disambiguationData":[OSD([sQuery(id+"F29.wireOp",EDGE,"E100.top")])]})],"blendedInto":[makeQuery(id+"F30.opExtrude","SWEPT_FACE",FACE,{"disambiguationData":[OSD([sQuery(id+"F29.wireOp",EDGE,"E100.top")])]})]});
            fillet(context, id + "F36", {"entities" : qUnion([Q0, Q1]), "radius" : 6 * mm, "tangentPropagation" : true, "allowEdgeOverflow" : false});
        }
    });
